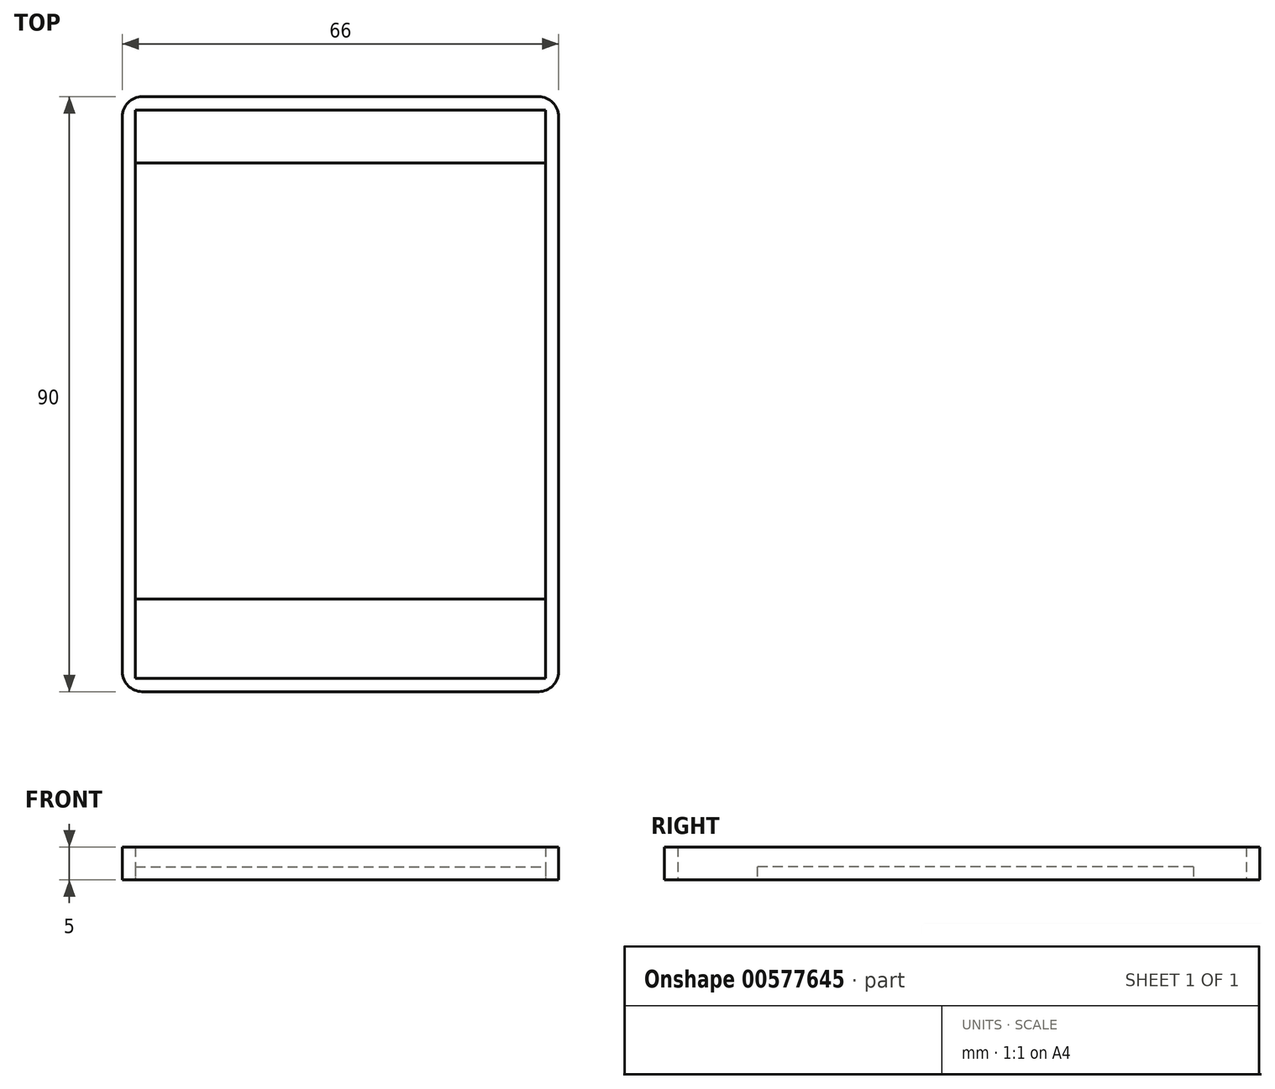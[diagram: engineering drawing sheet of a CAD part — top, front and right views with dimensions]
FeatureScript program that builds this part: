
annotation { "Feature Type Name" : "Feature", "Feature Type Description" : "" }
export const myFeature = defineFeature(function(context is Context, id is Id, definition is map)
    precondition{}
    {
        {
            var Q0;
            Q0=qCreatedBy(makeId("Top.planeOp"),FACE);
            var sketch = newSketch(context, id + "F0", { "sketchPlane" : qUnion([Q0])});
            skLineSegment(sketch, "E0.bottom", {"start": v(0, 0) * mm, "end": v(-62, 0) * mm});
            skLineSegment(sketch, "E0.top", {"start": v(0, -86) * mm, "end": v(-62, -86) * mm});
            skLineSegment(sketch, "E0.left", {"start": v(0, 0) * mm, "end": v(0, -86) * mm});
            skLineSegment(sketch, "E0.right", {"start": v(-62, 0) * mm, "end": v(-62, -86) * mm});
            skLineSegment(sketch, "E1.0", {"start": v(-1, 2) * mm, "end": v(-61, 2) * mm});
            skLineSegment(sketch, "E2.0", {"start": v(2, -1) * mm, "end": v(2, -85) * mm});
            skLineSegment(sketch, "E3.0", {"start": v(-1, -88) * mm, "end": v(-61, -88) * mm});
            skLineSegment(sketch, "E4.0", {"start": v(-64, -1) * mm, "end": v(-64, -85) * mm});
            skArc(sketch, "E5.filletArc", {"start": v(-61, 2) * mm, "mid": v(-63.12, 1.12) * mm, "end": v(-64, -1) * mm});
            skArc(sketch, "E6.filletArc", {"start": v(2, -1) * mm, "mid": v(1.12, 1.12) * mm, "end": v(-1, 2) * mm});
            skPoint(sketch, "E7.newPointB", {"position": v(0, -88) * mm});
            skArc(sketch, "E7.filletArc", {"start": v(-1, -88) * mm, "mid": v(1.12, -87.12) * mm, "end": v(2, -85) * mm});
            skPoint(sketch, "E8.newPointA", {"position": v(-62, -88) * mm});
            skArc(sketch, "E8.filletArc", {"start": v(-64, -85) * mm, "mid": v(-63.12, -87.12) * mm, "end": v(-61, -88) * mm});
            skLineSegment(sketch, "E9", {"start": v(-62, -8) * mm, "end": v(0, -8) * mm});
            skLineSegment(sketch, "E10", {"start": v(-62, -74) * mm, "end": v(0, -74) * mm});
            skSolve(sketch);
        }
        {
            var Q0;
            {var subQ6=sQuery(id+"F0.wireOp",EDGE,"E0.bottom");Q0=makeQuery(id+"F0.imprint","IMPRINT",FACE,{"disambiguationData":[TD([[makeQuery(id+"F0.imprint","IMPRINT",EDGE,{"derivedFrom":subQ6}),-1.0]])]});}
            extrude(context, id + "F1", {"entities" : qUnion([Q0]), "depth" : 5 * mm, "offsetDistance" : 25 * mm});
        }
        {
            var Q0;
            {var subQ0=sQuery(id+"F0.wireOp",EDGE,"E9");Q0=makeQuery(id+"F0.imprint","IMPRINT",FACE,{"disambiguationData":[TD([[makeQuery(id+"F0.imprint","IMPRINT",EDGE,{"derivedFrom":subQ0}),-1.0]])]});}
            extrude(context, id + "F2", {"entities" : qUnion([Q0]), "operationType" : NewBodyOperationType.ADD, "depth" : 2 * mm, "offsetDistance" : 25 * mm});
        }
    });
